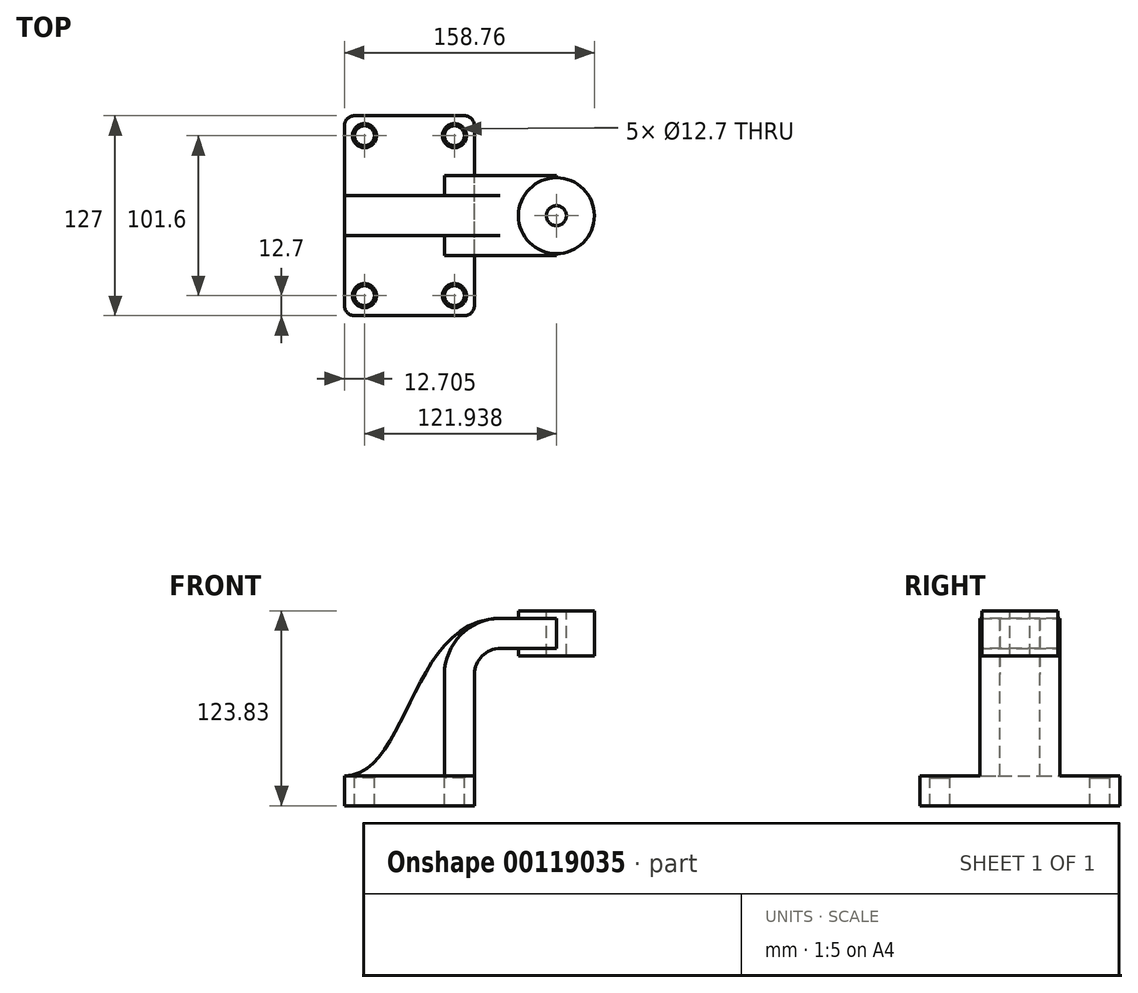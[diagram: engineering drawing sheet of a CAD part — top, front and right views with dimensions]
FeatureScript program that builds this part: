
annotation { "Feature Type Name" : "Feature", "Feature Type Description" : "" }
export const myFeature = defineFeature(function(context is Context, id is Id, definition is map)
    precondition{}
    {
        {
            var Q0;
            Q0=qCreatedBy(makeId("Front.planeOp"),FACE);
            var sketch = newSketch(context, id + "F0", { "sketchPlane" : qUnion([Q0])});
            skLineSegment(sketch, "E0.bottom", {"start": v(-41.28, -9.53) * mm, "end": v(41.28, -9.53) * mm});
            skLineSegment(sketch, "E0.top", {"start": v(-41.28, 9.53) * mm, "end": v(41.28, 9.53) * mm});
            skLineSegment(sketch, "E0.left", {"start": v(-41.28, -9.53) * mm, "end": v(-41.28, 9.53) * mm});
            skLineSegment(sketch, "E0.right", {"start": v(41.28, -9.53) * mm, "end": v(41.28, 9.53) * mm});
            skPoint(sketch, "E0.middle", {"position": v(0, 0) * mm});
            skLineSegment(sketch, "E1.bottom", {"start": v(117.47, 85.73) * mm, "end": v(66.67, 85.73) * mm});
            skLineSegment(sketch, "E1.top", {"start": v(117.47, 114.3) * mm, "end": v(66.67, 114.3) * mm});
            skLineSegment(sketch, "E1.left", {"start": v(117.48, 85.73) * mm, "end": v(117.48, 114.3) * mm});
            skLineSegment(sketch, "E1.right", {"start": v(66.68, 85.73) * mm, "end": v(66.67, 114.3) * mm});
            skLineSegment(sketch, "E2", {"start": v(41.27, 9.52) * mm, "end": v(41.27, 73.98) * mm});
            skArc(sketch, "E3", {"start": v(57.78, 90.49) * mm, "mid": v(46.11, 85.65) * mm, "end": v(41.27, 73.98) * mm});
            skLineSegment(sketch, "E4", {"start": v(57.78, 90.49) * mm, "end": v(93.36, 90.49) * mm});
            skLineSegment(sketch, "E5.0", {"start": v(57.78, 109.54) * mm, "end": v(93.36, 109.54) * mm});
            skArc(sketch, "E5.1", {"start": v(57.78, 109.54) * mm, "mid": v(32.64, 99.12) * mm, "end": v(22.22, 73.98) * mm});
            skLineSegment(sketch, "E5.2", {"start": v(22.22, 9.52) * mm, "end": v(22.22, 73.98) * mm});
            skLineSegment(sketch, "E6", {"start": v(93.36, 85.73) * mm, "end": v(93.36, 114.3) * mm});
            skFitSpline(sketch, "E7", {"points": [v(-41.28, 9.53) * mm, v(57.78, 109.54) * mm], "startDerivative": vector(123.83, 0) * mm, "endDerivative": vector(173.35, 0.3) * mm});
            skSolve(sketch);
        }
        {
            var Q0;
            Q0=makeQuery(id+"F0.imprint","IMPRINT",FACE,{"disambiguationData":[TD([[makeQuery(id+"F0.imprint","IMPRINT",EDGE,{"derivedFrom":sQuery(id+"F0.wireOp",EDGE,"E0.bottom")}),1.0]])]});
            extrude(context, id + "F1", {"entities" : qUnion([Q0]), "endBound" : BoundingType.SYMMETRIC, "depth" : 127 * mm});
        }
        {
            var Q0;
            {var subQ1=sQuery(id+"F0.wireOp",EDGE,"E2");Q0=makeQuery(id+"F0.imprint","IMPRINT",FACE,{"disambiguationData":[TD([[makeQuery(id+"F0.imprint","IMPRINT",EDGE,{"derivedFrom":subQ1}),1.0]])]});}
            var Q1;
            {var subQ0=sQuery(id+"F0.wireOp",EDGE,"E4");var subQ1=sQuery(id+"F0.wireOp",EDGE,"E1.right");var subQ2=makeQuery(id+"F0.imprint","INTERSECT",VERTEX,{"derivedFrom":[subQ1,subQ0]});Q1=makeQuery(id+"F0.imprint","IMPRINT",FACE,{"disambiguationData":[TD([[makeQuery(id+"F0.imprint","IMPRINT",EDGE,{"disambiguationData":[TD([[subQ2,-1.0]])],"derivedFrom":subQ1}),-1.0]])]});}
            extrude(context, id + "F2", {"entities" : qUnion([Q0, Q1]), "operationType" : NewBodyOperationType.ADD, "endBound" : BoundingType.SYMMETRIC, "depth" : 50.8 * mm});
        }
        {
            var Q0;
            {var subQ3=sQuery(id+"F0.wireOp",EDGE,"E5.2");Q0=makeQuery(id+"F0.imprint","IMPRINT",FACE,{"disambiguationData":[TD([[makeQuery(id+"F0.imprint","IMPRINT",EDGE,{"derivedFrom":subQ3}),1.0]])]});}
            extrude(context, id + "F3", {"entities" : qUnion([Q0]), "operationType" : NewBodyOperationType.ADD, "endBound" : BoundingType.SYMMETRIC, "depth" : 25.4 * mm});
        }
        {
            var Q0;
            {var subQ0=sQuery(id+"F0.wireOp",EDGE,"E1.left");Q0=makeQuery(id+"F0.imprint","IMPRINT",FACE,{"disambiguationData":[TD([[makeQuery(id+"F0.imprint","IMPRINT",EDGE,{"derivedFrom":subQ0}),1.0]])]});}
            var Q1;
            Q1=sQuery(id+"F0.wireOp",EDGE,"E6");
            revolve(context, id + "F4", {"operationType" : NewBodyOperationType.ADD, "entities" : qUnion([Q0]), "axis" : qUnion([Q1]), "revolveType" : RevolveType.FULL});
        }
        {
            var Q0;
            Q0=makeQuery(id+"F1.opExtrude","CAP_EDGE",EDGE,{"disambiguationData":[OSD([sQuery(id+"F0.wireOp",EDGE,"E0.left")])],"isStart":false});
            var Q1;
            Q1=makeQuery(id+"F1.opExtrude","CAP_EDGE",EDGE,{"disambiguationData":[OSD([sQuery(id+"F0.wireOp",EDGE,"E0.right")])],"isStart":false});
            var Q2;
            Q2=makeQuery(id+"F1.opExtrude","CAP_EDGE",EDGE,{"disambiguationData":[OSD([sQuery(id+"F0.wireOp",EDGE,"E0.left")])],"isStart":true});
            var Q3;
            Q3=makeQuery(id+"F1.opExtrude","CAP_EDGE",EDGE,{"disambiguationData":[OSD([sQuery(id+"F0.wireOp",EDGE,"E0.right")])],"isStart":true});
            fillet(context, id + "F5", {"entities" : qUnion([Q0, Q1, Q2, Q3]), "radius" : 6.35 * mm, "tangentPropagation" : true, "allowEdgeOverflow" : false});
        }
        {
            var Q0;
            Q0=makeQuery(id+"F4.opRevolve","SWEPT_FACE",FACE,{"disambiguationData":[OSD([sQuery(id+"F0.wireOp",EDGE,"E1.top")])]});
            var sketch = newSketch(context, id + "F6", { "sketchPlane" : qUnion([Q0])});
            skCircle(sketch, "E8", {"center": v(93.36, 0) * mm, "radius": 6.35 * mm});
            skSolve(sketch);
        }
        {
            var Q0;
            Q0=sQuery(id+"F6.wireOp",VERTEX,"E8.center");
            var Q1;
            Q1=makeQuery(id+"F1.opExtrude","SWEPT_BODY",BODY,{"disambiguationData":[OSD([sQuery(id+"F0.wireOp",EDGE,"E0.bottom"),sQuery(id+"F0.wireOp",EDGE,"E0.top"),sQuery(id+"F0.wireOp",EDGE,"E0.left"),sQuery(id+"F0.wireOp",EDGE,"E0.right")])]});
            hole(context, id + "F7", {"style" : HoleStyle.SIMPLE, "endStyle" : HoleEndStyle.THROUGH, "holeDiameter" : 12.7 * mm, "locations" : qUnion([Q0]), "scope" : qUnion([Q1]), "isTappedThrough" : true});
        }
        {
            var Q0;
            {var subQ4=sQuery(id+"F0.wireOp",EDGE,"E0.top");var subQ5=sQuery(id+"F0.wireOp",EDGE,"E0.right");var subQ6=sQuery(id+"F0.wireOp",EDGE,"E0.left");Q0=makeQuery(id+"F3.boolean.opBoolean","SPLIT",FACE,{"disambiguationData":[TD([makeQuery(id+"F1.opExtrude","CAP_FACE",FACE,{"disambiguationData":[OSD([sQuery(id+"F0.wireOp",EDGE,"E0.bottom"),subQ4,subQ6,subQ5])],"isStart":true})])],"derivedFrom":makeQuery(id+"F1.opExtrude","SWEPT_FACE",FACE,{"disambiguationData":[OSD([subQ4])]})});}
            var sketch = newSketch(context, id + "F8", { "sketchPlane" : qUnion([Q0])});
            skLineSegment(sketch, "E9.bottom", {"start": v(28.58, -50.8) * mm, "end": v(-28.57, -50.8) * mm});
            skLineSegment(sketch, "E9.top", {"start": v(28.57, 50.8) * mm, "end": v(-28.58, 50.8) * mm});
            skLineSegment(sketch, "E9.left", {"start": v(28.58, -50.8) * mm, "end": v(28.57, 50.8) * mm});
            skLineSegment(sketch, "E9.right", {"start": v(-28.57, -50.8) * mm, "end": v(-28.58, 50.8) * mm});
            skSolve(sketch);
        }
        {
            var Q0;
            Q0=sQuery(id+"F8.wireOp",VERTEX,"E9.right.start");
            var Q1;
            Q1=sQuery(id+"F8.wireOp",VERTEX,"E9.bottom.start");
            var Q2;
            Q2=sQuery(id+"F8.wireOp",VERTEX,"E9.left.end");
            var Q3;
            Q3=sQuery(id+"F8.wireOp",VERTEX,"E9.right.end");
            var Q4;
            Q4=makeQuery(id+"F1.opExtrude","SWEPT_BODY",BODY,{"disambiguationData":[OSD([sQuery(id+"F0.wireOp",EDGE,"E0.bottom"),sQuery(id+"F0.wireOp",EDGE,"E0.top"),sQuery(id+"F0.wireOp",EDGE,"E0.left"),sQuery(id+"F0.wireOp",EDGE,"E0.right")])]});
            hole(context, id + "F9", {"style" : HoleStyle.C_SINK, "endStyle" : HoleEndStyle.THROUGH, "holeDiameter" : 12.7 * mm, "cSinkDiameter" : 15.24 * mm, "cSinkAngle" : 90 * degree, "locations" : qUnion([Q0, Q1, Q2, Q3]), "scope" : qUnion([Q4]), "isTappedThrough" : true});
        }
    });
